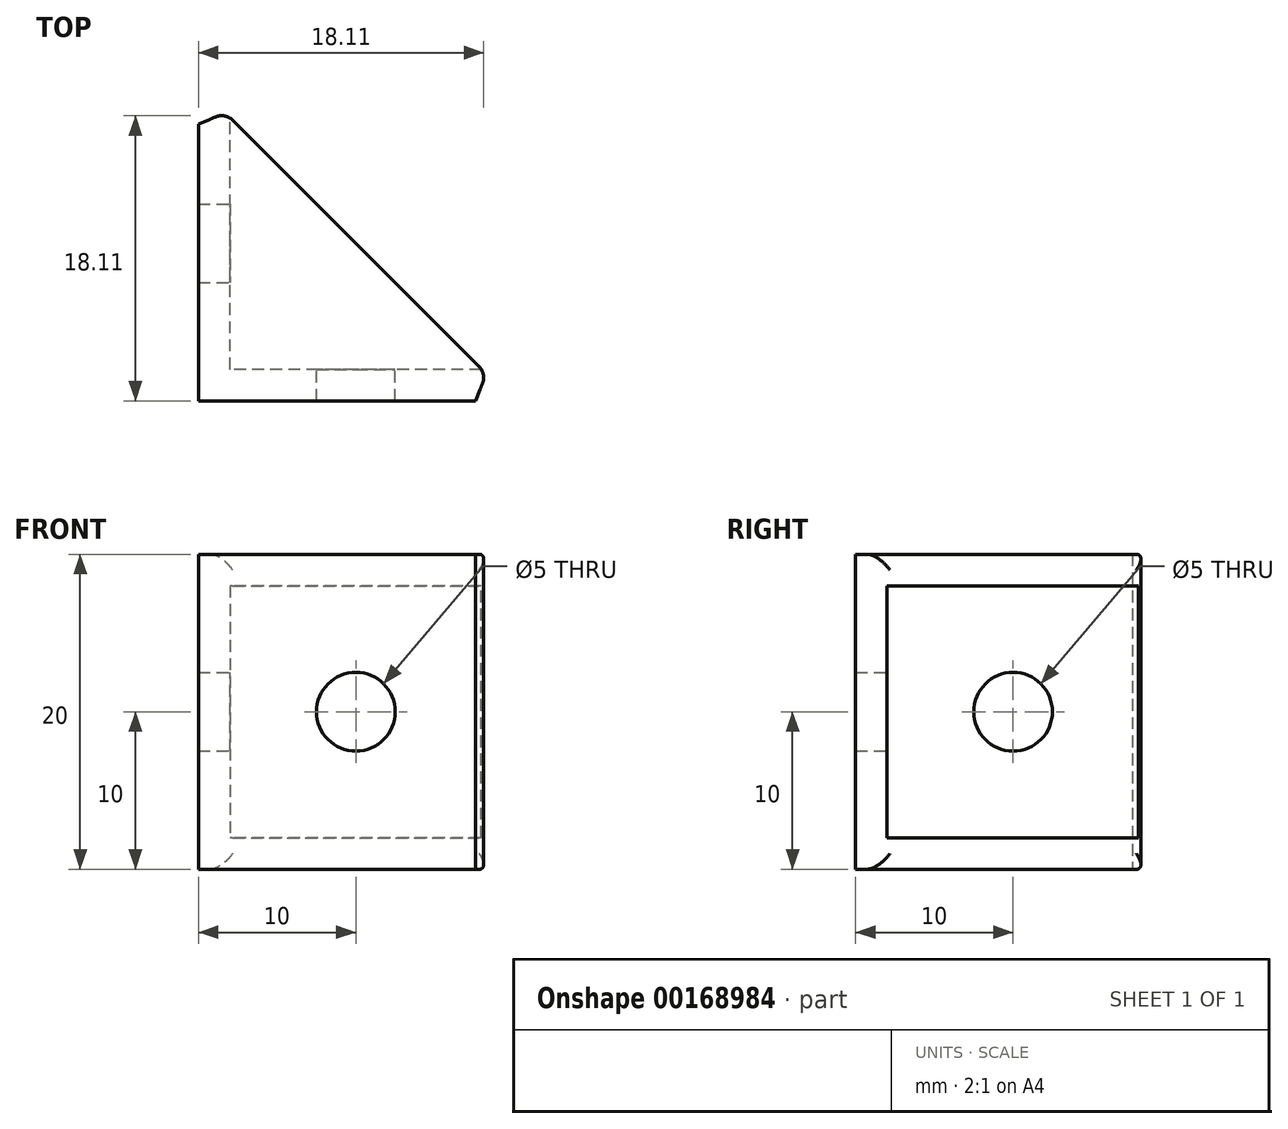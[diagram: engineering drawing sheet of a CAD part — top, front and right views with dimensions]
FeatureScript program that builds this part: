
annotation { "Feature Type Name" : "Feature", "Feature Type Description" : "" }
export const myFeature = defineFeature(function(context is Context, id is Id, definition is map)
    precondition{}
    {
        {
            var Q0;
            Q0=qCreatedBy(makeId("Top.planeOp"),FACE);
            var sketch = newSketch(context, id + "F6", { "sketchPlane" : qUnion([Q0])});
            skLineSegment(sketch, "E0.bottom", {"start": v(10, -10) * mm, "end": v(-10, -10) * mm});
            skLineSegment(sketch, "E0.top", {"start": v(10, 10) * mm, "end": v(-10, 10) * mm});
            skLineSegment(sketch, "E0.left", {"start": v(10, -10) * mm, "end": v(10, 10) * mm});
            skLineSegment(sketch, "E0.right", {"start": v(-10, -10) * mm, "end": v(-10, 10) * mm});
            skPoint(sketch, "E0.middle", {"position": v(0, 0) * mm});
            skLineSegment(sketch, "E1", {"start": v(-10, 10) * mm, "end": v(10, -10) * mm});
            skSolve(sketch);
        }
        {
            var Q0;
            Q0=makeQuery(id+"F6.imprint","IMPRINT",FACE,{"disambiguationData":[TD([[makeQuery(id+"F6.imprint","IMPRINT",EDGE,{"derivedFrom":sQuery(id+"F6.wireOp",EDGE,"E0.bottom")}),-1.0]])]});
            extrude(context, id + "F0", {"entities" : qUnion([Q0]), "depth" : 20 * mm});
        }
        {
            var Q0;
            Q0=makeQuery(id+"F0.opExtrude","SWEPT_FACE",FACE,{"disambiguationData":[OSD([sQuery(id+"F6.wireOp",EDGE,"E1")])]});
            shell(context, id + "F1", {"entities" : qUnion([Q0]), "thickness" : 2 * mm});
        }
        {
            var Q0;
            Q0=makeQuery(id+"F1.opShell","OFFSET_FACE",FACE,{"disambiguationData":[OSD([sQuery(id+"F6.wireOp",EDGE,"E0.right")])]});
            var sketch = newSketch(context, id + "F2", { "sketchPlane" : qUnion([Q0])});
            skPoint(sketch, "E2", {"position": v(0, 10) * mm});
            skPoint(sketch, "E2.positionSnap0", {"position": v(0, 2) * mm});
            skPoint(sketch, "E2.positionSnap1", {"position": v(8, 10) * mm});
            skSolve(sketch);
        }
        {
            var Q0;
            Q0=makeQuery(id+"F1.opShell","OFFSET_FACE",FACE,{"disambiguationData":[OSD([sQuery(id+"F6.wireOp",EDGE,"E0.bottom")])]});
            var sketch = newSketch(context, id + "F3", { "sketchPlane" : qUnion([Q0])});
            skPoint(sketch, "E3", {"position": v(0, 10) * mm});
            skPoint(sketch, "E3.positionSnap0", {"position": v(8, 10) * mm});
            skPoint(sketch, "E3.positionSnap1", {"position": v(0, 18) * mm});
            skSolve(sketch);
        }
        {
            var Q0;
            Q0=sQuery(id+"F3.wireOp",VERTEX,"E3");
            var Q1;
            Q1=sQuery(id+"F2.wireOp",VERTEX,"E2");
            var Q2;
            Q2=makeQuery(id+"F0.opExtrude","SWEPT_BODY",BODY,{"disambiguationData":[OSD([sQuery(id+"F6.wireOp",EDGE,"E0.bottom"),sQuery(id+"F6.wireOp",EDGE,"E0.right"),sQuery(id+"F6.wireOp",EDGE,"E1")])]});
            hole(context, id + "F4", {"style" : HoleStyle.SIMPLE, "endStyle" : HoleEndStyle.THROUGH, "holeDiameter" : 5 * mm, "locations" : qUnion([Q0, Q1]), "scope" : qUnion([Q2]), "isTappedThrough" : true});
        }
        {
            var Q0;
            Q0=makeQuery(id+"F0.opExtrude","SWEPT_EDGE",EDGE,{"disambiguationData":[OSD([sQuery(id+"F6.wireOp",EDGE,"E0.top"),sQuery(id+"F6.wireOp",EDGE,"E0.right"),sQuery(id+"F6.wireOp",EDGE,"E1")])]});
            var Q1;
            Q1=makeQuery(id+"F0.opExtrude","SWEPT_EDGE",EDGE,{"disambiguationData":[OSD([sQuery(id+"F6.wireOp",EDGE,"E0.bottom"),sQuery(id+"F6.wireOp",EDGE,"E0.left"),sQuery(id+"F6.wireOp",EDGE,"E1")])]});
            chamfer(context, id + "F5", {"entities" : qUnion([Q0, Q1]), "width" : 1 * mm, "tangentPropagation" : true});
        }
        {
            var Q0;
            Q0=makeQuery(id+"F0.opExtrude","CAP_EDGE",EDGE,{"disambiguationData":[OSD([sQuery(id+"F6.wireOp",EDGE,"E1")])],"isStart":true});
            var Q1;
            Q1=makeQuery(id+"F0.opExtrude","CAP_EDGE",EDGE,{"disambiguationData":[OSD([sQuery(id+"F6.wireOp",EDGE,"E1")])],"isStart":false});
            var Q2;
            {var subQ0=sQuery(id+"F6.wireOp",EDGE,"E1");Q2=makeQuery(id+"F5.opChamfer","BLEND_EDGE",EDGE,{"blendedFrom":[makeQuery(id+"F0.opExtrude","SWEPT_EDGE",EDGE,{"disambiguationData":[OSD([sQuery(id+"F6.wireOp",EDGE,"E0.bottom"),sQuery(id+"F6.wireOp",EDGE,"E0.left"),subQ0])]}),makeQuery(id+"F0.opExtrude","SWEPT_FACE",FACE,{"disambiguationData":[OSD([subQ0])]})],"blendedInto":[makeQuery(id+"F0.opExtrude","SWEPT_FACE",FACE,{"disambiguationData":[OSD([subQ0])]})]});}
            var Q3;
            {var subQ0=sQuery(id+"F6.wireOp",EDGE,"E1");Q3=makeQuery(id+"F5.opChamfer","BLEND_EDGE",EDGE,{"blendedFrom":[makeQuery(id+"F0.opExtrude","SWEPT_EDGE",EDGE,{"disambiguationData":[OSD([sQuery(id+"F6.wireOp",EDGE,"E0.top"),sQuery(id+"F6.wireOp",EDGE,"E0.right"),subQ0])]}),makeQuery(id+"F0.opExtrude","SWEPT_FACE",FACE,{"disambiguationData":[OSD([subQ0])]})],"blendedInto":[makeQuery(id+"F0.opExtrude","SWEPT_FACE",FACE,{"disambiguationData":[OSD([subQ0])]})]});}
            fillet(context, id + "F7", {"entities" : qUnion([Q0, Q1, Q2, Q3]), "radius" : 1 * mm, "tangentPropagation" : true, "allowEdgeOverflow" : false});
        }
    });
